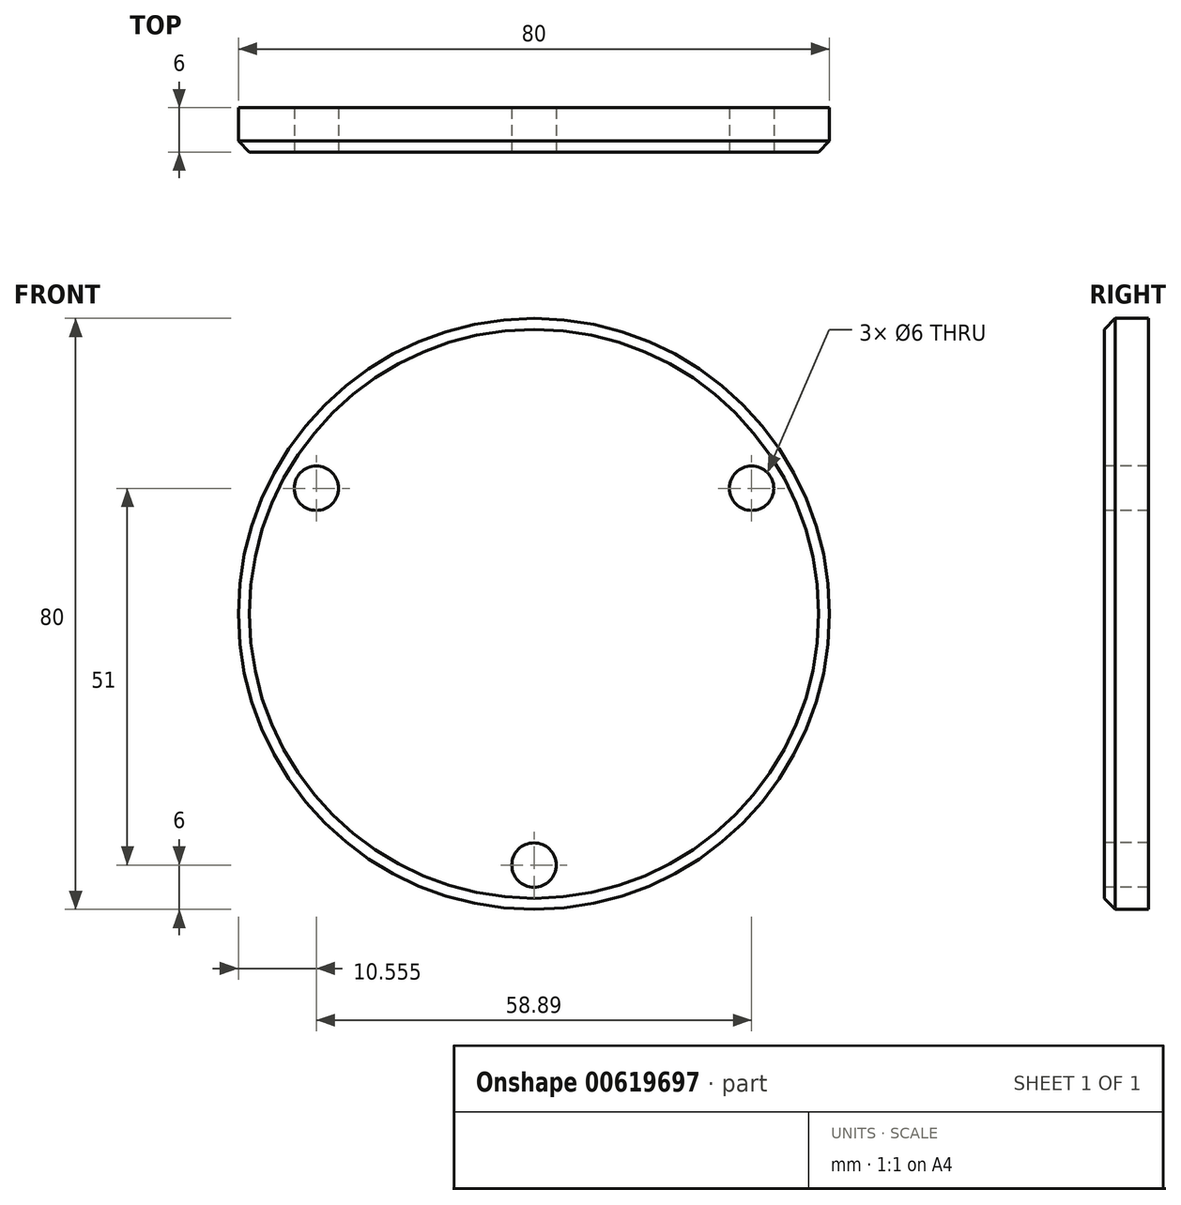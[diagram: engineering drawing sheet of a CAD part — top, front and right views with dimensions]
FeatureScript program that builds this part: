
annotation { "Feature Type Name" : "Feature", "Feature Type Description" : "" }
export const myFeature = defineFeature(function(context is Context, id is Id, definition is map)
    precondition{}
    {
        {
            var Q0;
            Q0=qCreatedBy(makeId("Front.planeOp"),FACE);
            var sketch = newSketch(context, id + "F0", { "sketchPlane" : qUnion([Q0])});
            skCircle(sketch, "E0", {"center": v(0, 0) * mm, "radius": 40 * mm});
            skSolve(sketch);
        }
        {
            var Q0;
            Q0 = qSketchRegion(id + "F0", true);
            extrude(context, id + "F1", {"entities" : qUnion([Q0]), "depth" : 6 * mm, "offsetDistance" : 25 * mm});
        }
        {
            var Q0;
            Q0=makeQuery(id+"F1.opExtrude","CAP_EDGE",EDGE,{"disambiguationData":[OSD([sQuery(id+"F0.wireOp",EDGE,"E0")])],"isStart":false});
            chamfer(context, id + "F2", {"entities" : qUnion([Q0]), "width" : 1.5 * mm, "tangentPropagation" : true});
        }
        {
            var Q0;
            Q0=makeQuery(id+"F1.opExtrude","CAP_FACE",FACE,{"disambiguationData":[OSD([sQuery(id+"F0.wireOp",EDGE,"E0")])],"isStart":false});
            var sketch = newSketch(context, id + "F3", { "sketchPlane" : qUnion([Q0])});
            skCircle(sketch, "E1", {"center": v(0, 0) * mm, "radius": 34 * mm});
            skCircle(sketch, "E2", {"center": v(0, -34) * mm, "radius": 3 * mm});
            skCircle(sketch, "E3", {"center": v(29.44, 17) * mm, "radius": 3 * mm});
            skCircle(sketch, "E4", {"center": v(-29.44, 17) * mm, "radius": 3 * mm});
            skLineSegment(sketch, "E5", {"start": v(0, 0) * mm, "end": v(0, -34) * mm});
            skLineSegment(sketch, "E6", {"start": v(0, 0) * mm, "end": v(29.44, 17) * mm});
            skLineSegment(sketch, "E7", {"start": v(-29.44, 17) * mm, "end": v(0, 0) * mm});
            skSolve(sketch);
        }
        {
            var Q0;
            {var subQ0=sQuery(id+"F3.wireOp",EDGE,"E1");var subQ1=makeQuery(id+"F3.imprint","INTERSECT",VERTEX,{"derivedFrom":[subQ0,sQuery(id+"F3.wireOp",EDGE,"E7")]});Q0=makeQuery(id+"F3.imprint","IMPRINT",FACE,{"disambiguationData":[TD([[makeQuery(id+"F3.imprint","IMPRINT",EDGE,{"disambiguationData":[TD([[subQ1,1.0]])],"derivedFrom":subQ0}),-1.0]])]});}
            var Q1;
            {var subQ0=sQuery(id+"F3.wireOp",EDGE,"E7");var subQ1=sQuery(id+"F3.wireOp",EDGE,"E1");var subQ2=makeQuery(id+"F3.imprint","INTERSECT",VERTEX,{"derivedFrom":[subQ1,subQ0]});Q1=makeQuery(id+"F3.imprint","IMPRINT",FACE,{"disambiguationData":[TD([[makeQuery(id+"F3.imprint","IMPRINT",EDGE,{"disambiguationData":[TD([[subQ2,1.0]])],"derivedFrom":subQ1}),1.0]])]});}
            var Q2;
            {var subQ0=sQuery(id+"F3.wireOp",EDGE,"E7");var subQ1=sQuery(id+"F3.wireOp",EDGE,"E1");var subQ2=makeQuery(id+"F3.imprint","INTERSECT",VERTEX,{"derivedFrom":[subQ1,subQ0]});Q2=makeQuery(id+"F3.imprint","IMPRINT",FACE,{"disambiguationData":[TD([[makeQuery(id+"F3.imprint","IMPRINT",EDGE,{"disambiguationData":[TD([[subQ2,-1.0]])],"derivedFrom":subQ1}),1.0]])]});}
            var Q3;
            {var subQ0=sQuery(id+"F3.wireOp",EDGE,"E1");var subQ1=makeQuery(id+"F3.imprint","INTERSECT",VERTEX,{"derivedFrom":[subQ0,sQuery(id+"F3.wireOp",EDGE,"E6")]});Q3=makeQuery(id+"F3.imprint","IMPRINT",FACE,{"disambiguationData":[TD([[makeQuery(id+"F3.imprint","IMPRINT",EDGE,{"disambiguationData":[TD([[subQ1,1.0]])],"derivedFrom":subQ0}),-1.0]])]});}
            var Q4;
            {var subQ0=sQuery(id+"F3.wireOp",EDGE,"E6");var subQ1=sQuery(id+"F3.wireOp",EDGE,"E1");var subQ2=makeQuery(id+"F3.imprint","INTERSECT",VERTEX,{"derivedFrom":[subQ1,subQ0]});Q4=makeQuery(id+"F3.imprint","IMPRINT",FACE,{"disambiguationData":[TD([[makeQuery(id+"F3.imprint","IMPRINT",EDGE,{"disambiguationData":[TD([[subQ2,-1.0]])],"derivedFrom":subQ1}),1.0]])]});}
            var Q5;
            {var subQ0=sQuery(id+"F3.wireOp",EDGE,"E6");var subQ1=sQuery(id+"F3.wireOp",EDGE,"E1");var subQ2=makeQuery(id+"F3.imprint","INTERSECT",VERTEX,{"derivedFrom":[subQ1,subQ0]});Q5=makeQuery(id+"F3.imprint","IMPRINT",FACE,{"disambiguationData":[TD([[makeQuery(id+"F3.imprint","IMPRINT",EDGE,{"disambiguationData":[TD([[subQ2,1.0]])],"derivedFrom":subQ1}),1.0]])]});}
            var Q6;
            {var subQ0=sQuery(id+"F3.wireOp",EDGE,"E5");var subQ1=sQuery(id+"F3.wireOp",EDGE,"E1");var subQ2=makeQuery(id+"F3.imprint","INTERSECT",VERTEX,{"derivedFrom":[subQ1,subQ0]});Q6=makeQuery(id+"F3.imprint","IMPRINT",FACE,{"disambiguationData":[TD([[makeQuery(id+"F3.imprint","IMPRINT",EDGE,{"disambiguationData":[TD([[subQ2,-1.0]])],"derivedFrom":subQ1}),1.0]])]});}
            var Q7;
            {var subQ0=sQuery(id+"F3.wireOp",EDGE,"E5");var subQ1=sQuery(id+"F3.wireOp",EDGE,"E1");var subQ2=makeQuery(id+"F3.imprint","INTERSECT",VERTEX,{"derivedFrom":[subQ1,subQ0]});Q7=makeQuery(id+"F3.imprint","IMPRINT",FACE,{"disambiguationData":[TD([[makeQuery(id+"F3.imprint","IMPRINT",EDGE,{"disambiguationData":[TD([[subQ2,1.0]])],"derivedFrom":subQ1}),1.0]])]});}
            var Q8;
            {var subQ0=sQuery(id+"F3.wireOp",EDGE,"E1");var subQ1=makeQuery(id+"F3.imprint","INTERSECT",VERTEX,{"derivedFrom":[subQ0,sQuery(id+"F3.wireOp",EDGE,"E5")]});Q8=makeQuery(id+"F3.imprint","IMPRINT",FACE,{"disambiguationData":[TD([[makeQuery(id+"F3.imprint","IMPRINT",EDGE,{"disambiguationData":[TD([[subQ1,1.0]])],"derivedFrom":subQ0}),-1.0]])]});}
            extrude(context, id + "F4", {"entities" : qUnion([Q0, Q1, Q2, Q3, Q4, Q5, Q6, Q7, Q8]), "operationType" : NewBodyOperationType.REMOVE, "oppositeDirection" : true, "depth" : 25 * mm, "offsetDistance" : 25 * mm});
        }
    });
